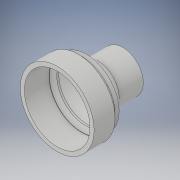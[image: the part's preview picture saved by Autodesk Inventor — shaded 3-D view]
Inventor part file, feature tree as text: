
AUTODESK INVENTOR PART (.ipt)
format: ipt  version: 2019 (Build 230136000, 136)  size: 156,672 bytes
history: native  units: mm
features: extrude x5, chamfer x4, sketch x3
ambient origin geometry x8: Origin, YZ Plane, XZ Plane, XY Plane, X Axis, Y Axis, Z Axis, Center Point
bodies: Solid1 (feature_tree)
feature tree (12):
  sketch  "Sketch1"  dims[d0=40.0mm d1=45.0mm]
  extrude  "Extrusion1"  Depth=40.0mm
  extrude  "Extrusion2"  Depth=10.0mm TaperAngle=0.0deg
  sketch  "Sketch2"  dims[d2=15.0mm d3=0.0mm d4=10.0mm d5=0.0mm]
  extrude  "Extrusion3"  Depth=20.0mm
  chamfer  "Chamfer1"  Distance=15.0mm
  chamfer  "Chamfer2"  Distance=7.25mm Angle=45.0deg
  extrude  "Extrusion4"  Depth=15.0mm TaperAngle=45.0deg
  extrude  "Extrusion5"  Depth=15.0mm TaperAngle=0.0deg
  chamfer  "Chamfer3"  Distance=35.0mm
  chamfer  "Chamfer4"  Distance=3.5mm
  sketch  "Sketch3"  dims[d6=25.0mm d7=20.0mm d8=15.0mm d9=0.0mm d10=7.25mm d11=2.0mm d12=45.0deg d13=2.25mm d14=2.0mm d15=45.0deg d16=15.0mm d17=0.0mm d18=35.0mm d19=3.5mm d20=0.0mm d21=7.5mm d22=2.0mm d23=45.0deg d24=2.25mm d25=2.0mm d26=45.0deg]
